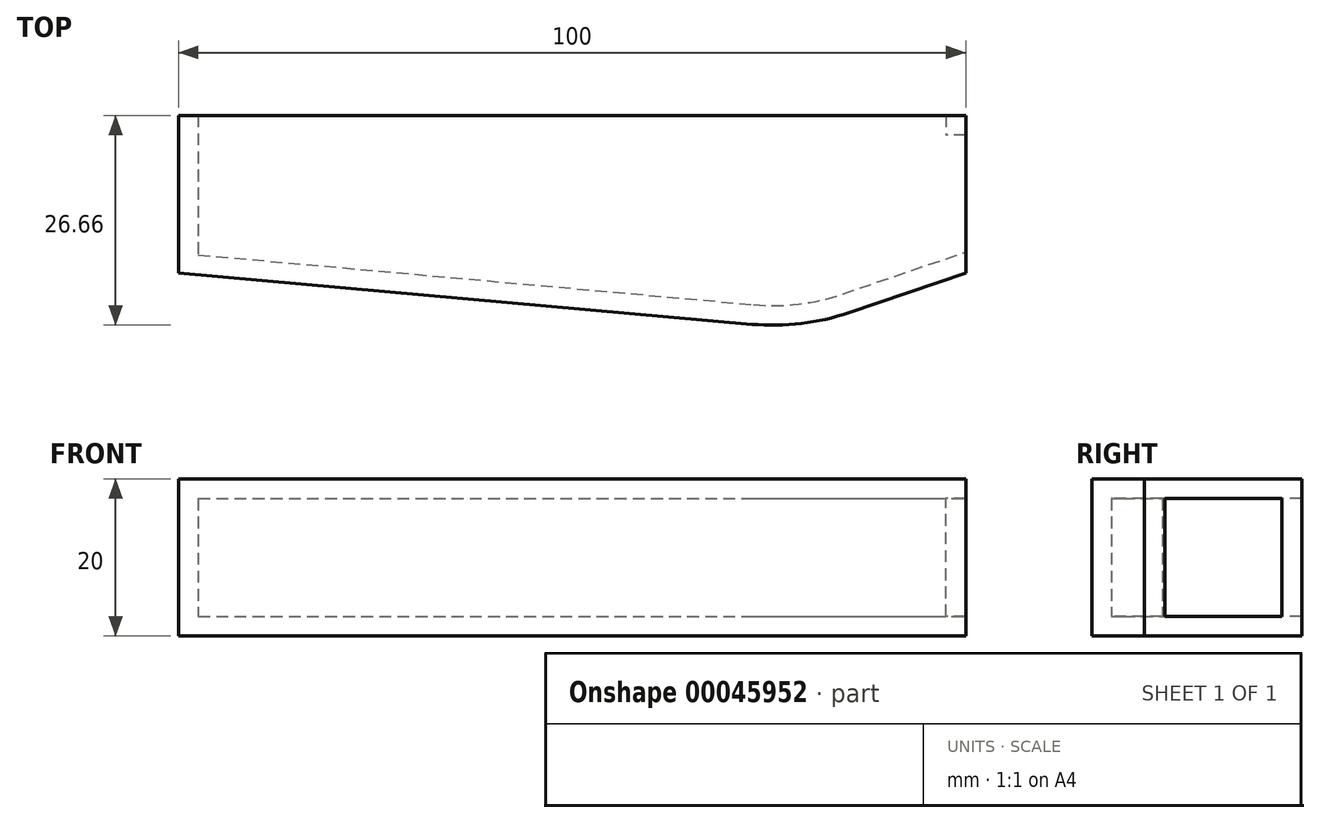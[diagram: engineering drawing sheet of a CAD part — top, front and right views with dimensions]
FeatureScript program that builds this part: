
annotation { "Feature Type Name" : "Feature", "Feature Type Description" : "" }
export const myFeature = defineFeature(function(context is Context, id is Id, definition is map)
    precondition{}
    {
        {
            var Q0;
            Q0=qCreatedBy(makeId("Top.planeOp"),FACE);
            var sketch = newSketch(context, id + "F0", { "sketchPlane" : qUnion([Q0])});
            skLineSegment(sketch, "E0", {"start": v(-55.74, 20) * mm, "end": v(-55.74, 0) * mm});
            skLineSegment(sketch, "E1", {"start": v(-55.74, 20) * mm, "end": v(44.26, 20) * mm});
            skLineSegment(sketch, "E2", {"start": v(44.26, 20) * mm, "end": v(44.26, 0) * mm});
            skLineSegment(sketch, "E3", {"start": v(-55.74, 0) * mm, "end": v(23.42, -7.1) * mm});
            skLineSegment(sketch, "E4", {"start": v(23.42, -7.1) * mm, "end": v(44.26, 0) * mm});
            skSolve(sketch);
        }
        {
            var Q0;
            Q0 = qSketchRegion(id + "F0", true);
            extrude(context, id + "F1", {"entities" : qUnion([Q0]), "depth" : 20 * mm});
        }
        {
            var Q0;
            Q0=makeQuery(id+"F1.opExtrude","SWEPT_EDGE",EDGE,{"disambiguationData":[OSD([sQuery(id+"F0.wireOp",EDGE,"E3"),sQuery(id+"F0.wireOp",EDGE,"E4")])]});
            fillet(context, id + "F2", {"entities" : qUnion([Q0]), "radius" : 30 * mm, "tangentPropagation" : true, "allowEdgeOverflow" : false});
        }
        {
            var Q0;
            Q0=makeQuery(id+"F1.opExtrude","SWEPT_FACE",FACE,{"disambiguationData":[OSD([sQuery(id+"F0.wireOp",EDGE,"E2")])]});
            var Q1;
            Q1=makeQuery(id+"F1.opExtrude","SWEPT_FACE",FACE,{"disambiguationData":[OSD([sQuery(id+"F0.wireOp",EDGE,"E1")])]});
            shell(context, id + "F3", {"entities" : qUnion([Q0, Q1]), "thickness" : 2.5 * mm});
        }
        {
            var Q0;
            {var subQ0=sQuery(id+"F0.wireOp",EDGE,"E0");var subQ1=sQuery(id+"F0.wireOp",EDGE,"E1");var subQ2=sQuery(id+"F0.wireOp",EDGE,"E2");var subQ3=sQuery(id+"F0.wireOp",EDGE,"E3");var subQ4=sQuery(id+"F0.wireOp",EDGE,"E4");Q0=makeQuery(id+"F3.opShell","OFFSET_FACE",FACE,{"disambiguationData":[OSD([subQ0,subQ1,subQ2,subQ3,subQ4]),TDD([makeQuery(id+"F1.opExtrude","CAP_FACE",FACE,{"disambiguationData":[OSD([subQ0,subQ1,subQ2,subQ3,subQ4])],"isStart":false})])]});}
            var sketch = newSketch(context, id + "F4", { "sketchPlane" : qUnion([Q0])});
            skLineSegment(sketch, "E5.bottom", {"start": v(44.26, -20) * mm, "end": v(41.76, -20) * mm});
            skLineSegment(sketch, "E5.top", {"start": v(44.26, -17.5) * mm, "end": v(41.76, -17.5) * mm});
            skLineSegment(sketch, "E5.left", {"start": v(44.26, -20) * mm, "end": v(44.26, -17.5) * mm});
            skLineSegment(sketch, "E5.right", {"start": v(41.76, -20) * mm, "end": v(41.76, -17.5) * mm});
            skSolve(sketch);
        }
        {
            var Q0;
            Q0 = qSketchRegion(id + "F4", true);
            extrude(context, id + "F5", {"entities" : qUnion([Q0]), "operationType" : NewBodyOperationType.ADD, "depth" : 15 * mm});
        }
    });
